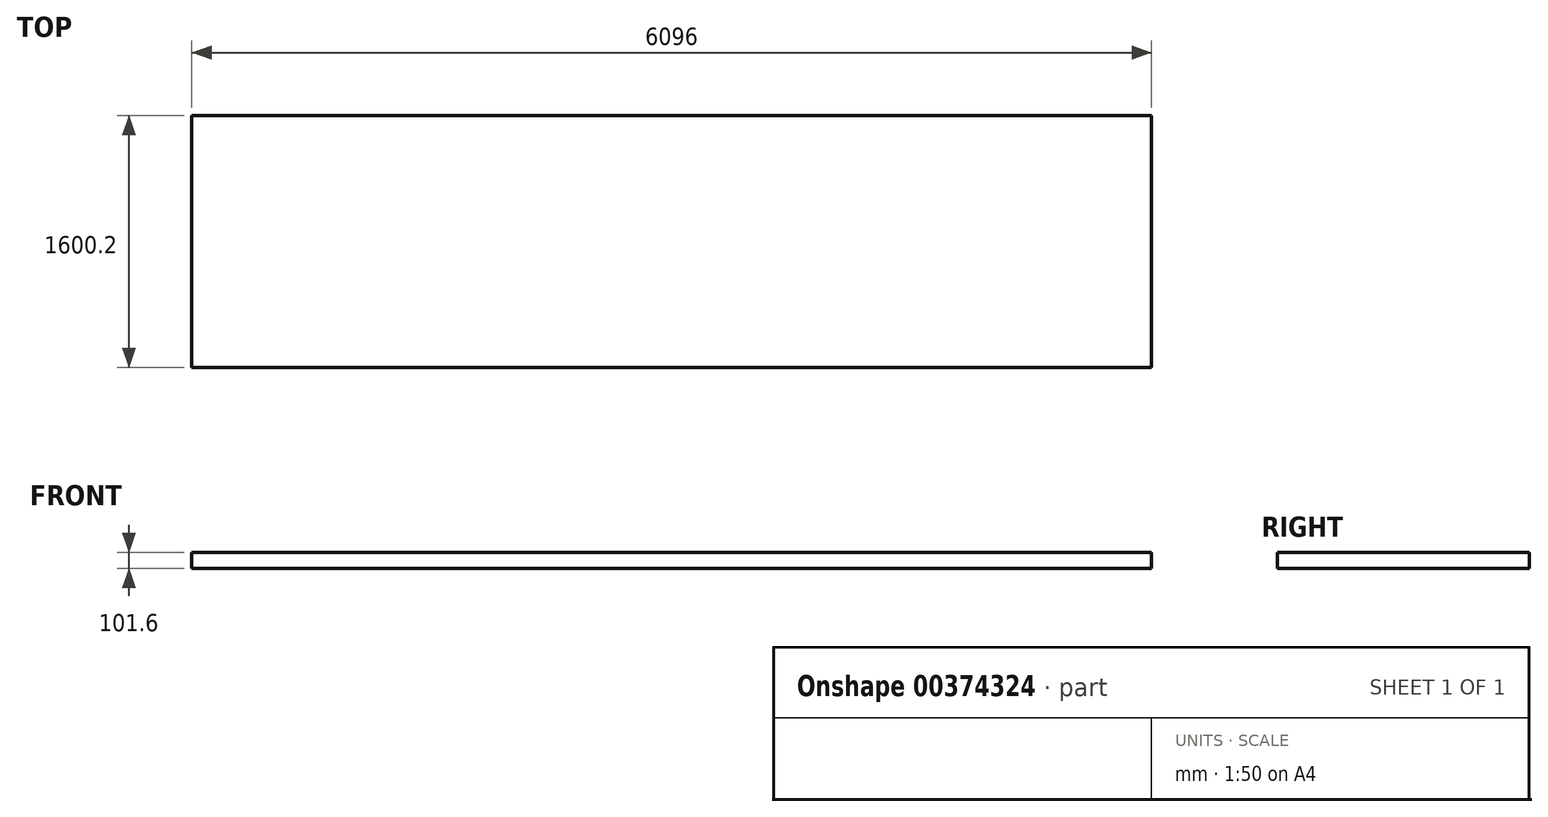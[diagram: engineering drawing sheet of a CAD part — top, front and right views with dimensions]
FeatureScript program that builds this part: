
annotation { "Feature Type Name" : "Feature", "Feature Type Description" : "" }
export const myFeature = defineFeature(function(context is Context, id is Id, definition is map)
    precondition{}
    {
        {
            var Q0;
            Q0=qCreatedBy(makeId("Top.planeOp"),FACE);
            var sketch = newSketch(context, id + "F0", { "sketchPlane" : qUnion([Q0])});
            skLineSegment(sketch, "E0.bottom", {"start": v(3048, -800.1) * mm, "end": v(-3048, -800.1) * mm});
            skLineSegment(sketch, "E0.top", {"start": v(3048, 800.1) * mm, "end": v(-3048, 800.1) * mm});
            skLineSegment(sketch, "E0.left", {"start": v(3048, -800.1) * mm, "end": v(3048, 800.1) * mm});
            skLineSegment(sketch, "E0.right", {"start": v(-3048, -800.1) * mm, "end": v(-3048, 800.1) * mm});
            skPoint(sketch, "E0.middle", {"position": v(0, 0) * mm});
            skSolve(sketch);
        }
        {
            var Q0;
            Q0=makeQuery(id+"F0.imprint","IMPRINT",FACE,{"disambiguationData":[TD([[makeQuery(id+"F0.imprint","IMPRINT",EDGE,{"derivedFrom":sQuery(id+"F0.wireOp",EDGE,"E0.bottom")}),-1.0]])]});
            extrude(context, id + "F1", {"entities" : qUnion([Q0]), "oppositeDirection" : true, "depth" : 101.6 * mm});
        }
    });
